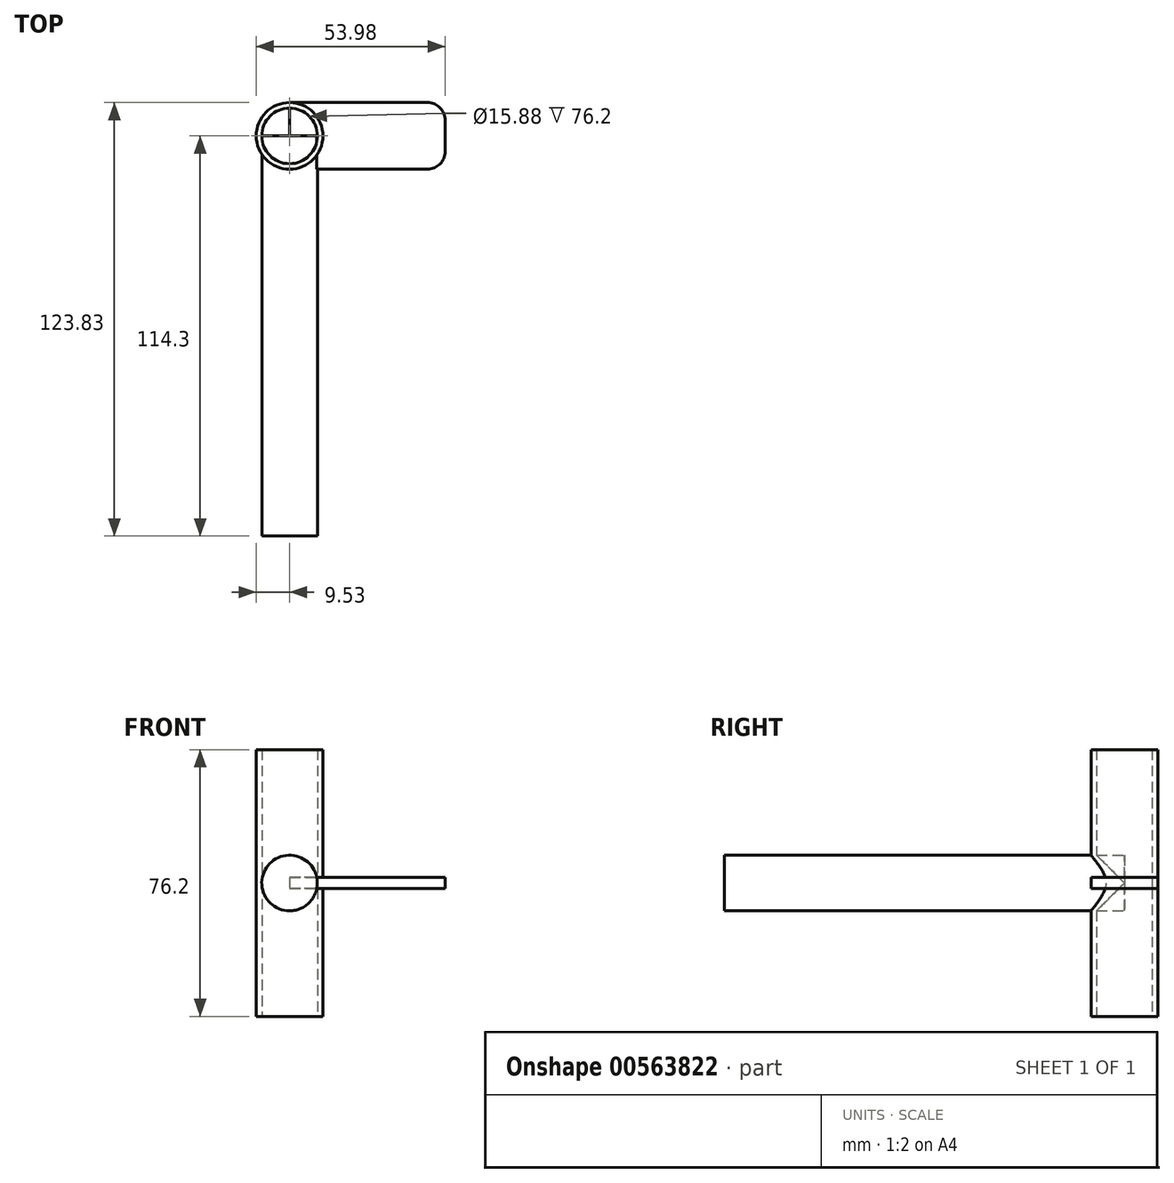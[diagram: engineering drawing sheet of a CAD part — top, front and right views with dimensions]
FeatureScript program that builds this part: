
annotation { "Feature Type Name" : "Feature", "Feature Type Description" : "" }
export const myFeature = defineFeature(function(context is Context, id is Id, definition is map)
    precondition{}
    {
        {
            var Q0;
            Q0=qCreatedBy(makeId("Top.planeOp"),FACE);
            var sketch = newSketch(context, id + "F0", { "sketchPlane" : qUnion([Q0])});
            skCircle(sketch, "E0", {"center": v(0, 0) * mm, "radius": 9.53 * mm});
            skCircle(sketch, "E1", {"center": v(0, 0) * mm, "radius": 7.94 * mm});
            skSolve(sketch);
        }
        {
            var Q0;
            Q0=makeQuery(id+"F0.imprint","IMPRINT",FACE,{"disambiguationData":[TD([[makeQuery(id+"F0.imprint","IMPRINT",EDGE,{"derivedFrom":sQuery(id+"F0.wireOp",EDGE,"E0")}),1.0]])]});
            extrude(context, id + "F1", {"entities" : qUnion([Q0]), "endBound" : BoundingType.SYMMETRIC, "depth" : 76.2 * mm, "offsetDistance" : 25.4 * mm});
        }
        {
            var Q0;
            Q0=qCreatedBy(makeId("Right.planeOp"),FACE);
            var sketch = newSketch(context, id + "F2", { "sketchPlane" : qUnion([Q0])});
            skLineSegment(sketch, "E2.bottom", {"start": v(9.53, 1.59) * mm, "end": v(-9.53, 1.59) * mm});
            skLineSegment(sketch, "E2.top", {"start": v(9.53, -1.59) * mm, "end": v(-9.53, -1.59) * mm});
            skLineSegment(sketch, "E2.left", {"start": v(9.53, 1.59) * mm, "end": v(9.53, -1.59) * mm});
            skLineSegment(sketch, "E2.right", {"start": v(-9.53, 1.59) * mm, "end": v(-9.53, -1.59) * mm});
            skPoint(sketch, "E2.middle", {"position": v(0, 0) * mm});
            skSolve(sketch);
        }
        {
            var Q0;
            Q0 = qSketchRegion(id + "F2", true);
            extrude(context, id + "F3", {"entities" : qUnion([Q0]), "operationType" : NewBodyOperationType.ADD, "depth" : 44.45 * mm, "offsetDistance" : 25.4 * mm});
        }
        {
            var Q0;
            Q0=makeQuery(id+"F3.opExtrude","CAP_EDGE",EDGE,{"disambiguationData":[OSD([sQuery(id+"F2.wireOp",EDGE,"E2.right")])],"isStart":false});
            var Q1;
            Q1=makeQuery(id+"F3.opExtrude","CAP_EDGE",EDGE,{"disambiguationData":[OSD([sQuery(id+"F2.wireOp",EDGE,"E2.left")])],"isStart":false});
            fillet(context, id + "F4", {"entities" : qUnion([Q0, Q1]), "radius" : 5.08 * mm, "tangentPropagation" : true, "allowEdgeOverflow" : false});
        }
        {
            var Q0;
            Q0=qCreatedBy(makeId("Front.planeOp"),FACE);
            var sketch = newSketch(context, id + "F5", { "sketchPlane" : qUnion([Q0])});
            skCircle(sketch, "E3", {"center": v(0, 0) * mm, "radius": 7.94 * mm});
            skSolve(sketch);
        }
        {
            var Q0;
            Q0 = qSketchRegion(id + "F5", true);
            extrude(context, id + "F6", {"entities" : qUnion([Q0]), "operationType" : NewBodyOperationType.ADD, "depth" : 114.3 * mm, "offsetDistance" : 25.4 * mm});
        }
    });
